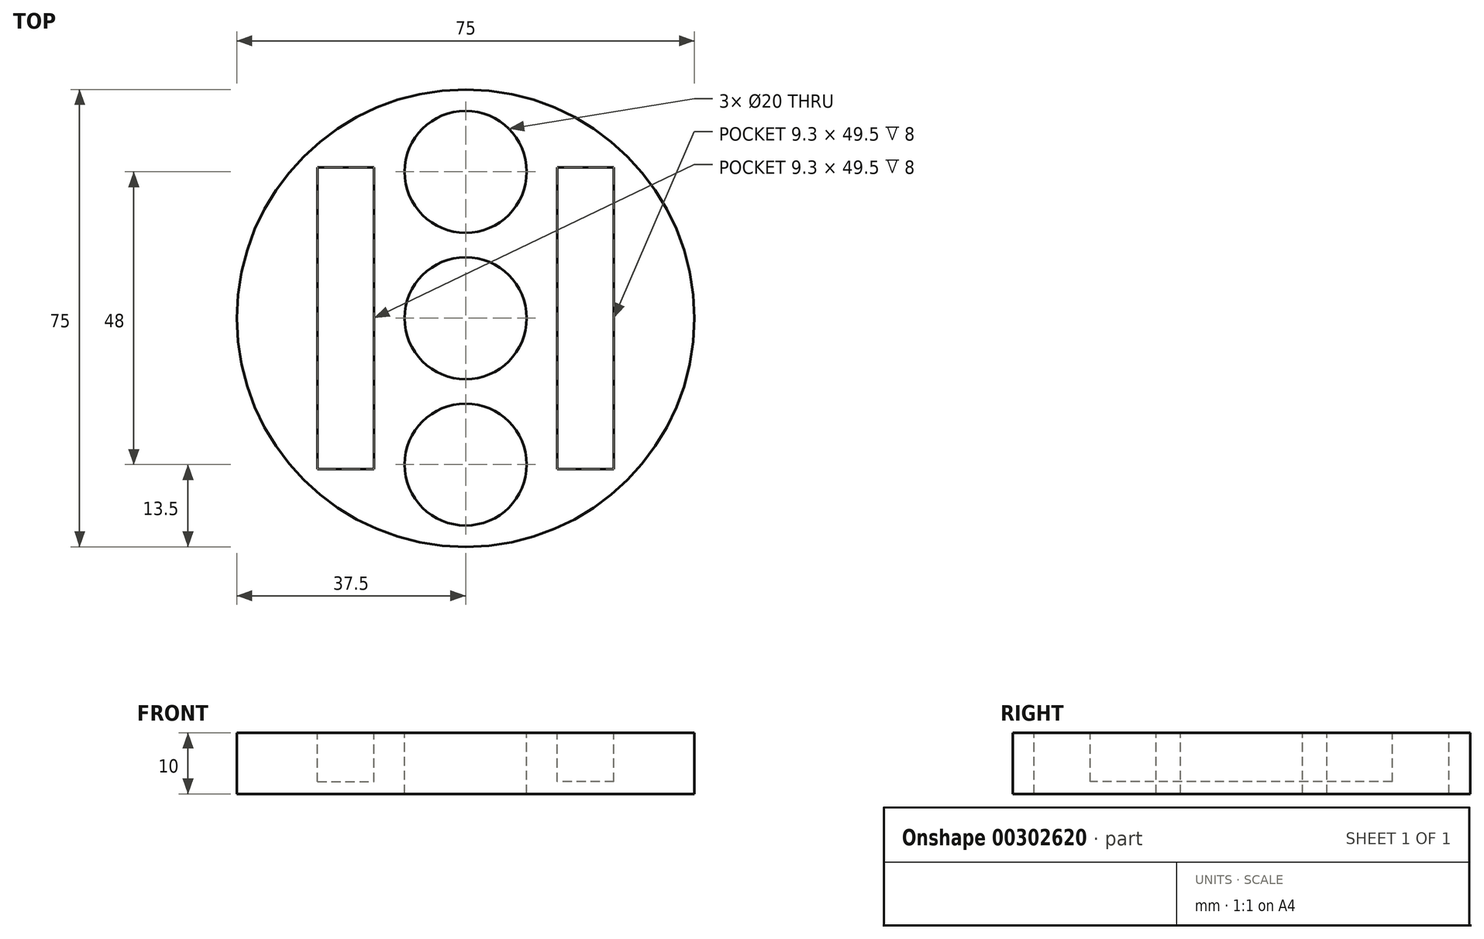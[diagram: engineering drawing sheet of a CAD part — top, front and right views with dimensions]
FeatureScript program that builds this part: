
annotation { "Feature Type Name" : "Feature", "Feature Type Description" : "" }
export const myFeature = defineFeature(function(context is Context, id is Id, definition is map)
    precondition{}
    {
        {
            var Q0;
            Q0=qCreatedBy(makeId("Top.planeOp"),FACE);
            var sketch = newSketch(context, id + "F0", { "sketchPlane" : qUnion([Q0])});
            skCircle(sketch, "E0", {"center": v(0, 0) * mm, "radius": 37.5 * mm});
            skSolve(sketch);
        }
        {
            var Q0;
            Q0 = qSketchRegion(id + "F0", true);
            extrude(context, id + "F1", {"entities" : qUnion([Q0]), "depth" : (10) * mm});
        }
        {
            var Q0;
            Q0=makeQuery(id+"F1.opExtrude","CAP_FACE",FACE,{"disambiguationData":[OSD([sQuery(id+"F0.wireOp",EDGE,"E0")])],"isStart":false});
            var sketch = newSketch(context, id + "F2", { "sketchPlane" : qUnion([Q0])});
            skLineSegment(sketch, "E1.bottom", {"start": v(24.3, 24.75) * mm, "end": v(15, 24.75) * mm});
            skLineSegment(sketch, "E1.top", {"start": v(24.3, -24.75) * mm, "end": v(15, -24.75) * mm});
            skLineSegment(sketch, "E1.left", {"start": v(24.3, 24.75) * mm, "end": v(24.3, -24.75) * mm});
            skLineSegment(sketch, "E1.right", {"start": v(15, 24.75) * mm, "end": v(15, -24.75) * mm});
            skPoint(sketch, "E1.middle", {"position": v(19.65, 0) * mm});
            skLineSegment(sketch, "E2.MirrorCS", {"start": v(-15, 24.75) * mm, "end": v(-15, -24.75) * mm});
            skLineSegment(sketch, "E3.MirrorCS", {"start": v(-24.3, 24.75) * mm, "end": v(-24.3, -24.75) * mm});
            skLineSegment(sketch, "E4.MirrorCS", {"start": v(-24.3, -24.75) * mm, "end": v(-15, -24.75) * mm});
            skLineSegment(sketch, "E5.MirrorCS", {"start": v(-24.3, 24.75) * mm, "end": v(-15, 24.75) * mm});
            skCircle(sketch, "E6", {"center": v(0, 0) * mm, "radius": 10 * mm});
            skCircle(sketch, "E7", {"center": v(0, 24) * mm, "radius": 10 * mm});
            skCircle(sketch, "E8", {"center": v(0, -24) * mm, "radius": 10 * mm});
            skSolve(sketch);
        }
        {
            var Q0;
            Q0=makeQuery(id+"F2.imprint","IMPRINT",FACE,{"disambiguationData":[TD([[makeQuery(id+"F2.imprint","IMPRINT",EDGE,{"derivedFrom":sQuery(id+"F2.wireOp",EDGE,"E2.MirrorCS")}),-1.0]])]});
            var Q1;
            Q1=makeQuery(id+"F2.imprint","IMPRINT",FACE,{"disambiguationData":[TD([[makeQuery(id+"F2.imprint","IMPRINT",EDGE,{"derivedFrom":sQuery(id+"F2.wireOp",EDGE,"E1.bottom")}),1.0]])]});
            extrude(context, id + "F3", {"entities" : qUnion([Q0, Q1]), "operationType" : NewBodyOperationType.REMOVE, "oppositeDirection" : true, "depth" : (8) * mm});
        }
        {
            var Q0;
            Q0=makeQuery(id+"F2.imprint","IMPRINT",FACE,{"disambiguationData":[TD([[makeQuery(id+"F2.imprint","IMPRINT",EDGE,{"derivedFrom":sQuery(id+"F2.wireOp",EDGE,"E7")}),1.0]])]});
            var Q1;
            Q1=makeQuery(id+"F2.imprint","IMPRINT",FACE,{"disambiguationData":[TD([[makeQuery(id+"F2.imprint","IMPRINT",EDGE,{"derivedFrom":sQuery(id+"F2.wireOp",EDGE,"E6")}),1.0]])]});
            var Q2;
            Q2=makeQuery(id+"F2.imprint","IMPRINT",FACE,{"disambiguationData":[TD([[makeQuery(id+"F2.imprint","IMPRINT",EDGE,{"derivedFrom":sQuery(id+"F2.wireOp",EDGE,"E8")}),1.0]])]});
            extrude(context, id + "F4", {"entities" : qUnion([Q0, Q1, Q2]), "operationType" : NewBodyOperationType.REMOVE, "endBound" : BoundingType.THROUGH_ALL, "oppositeDirection" : true, "depth" : 25 * mm});
        }
    });
